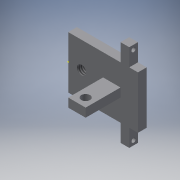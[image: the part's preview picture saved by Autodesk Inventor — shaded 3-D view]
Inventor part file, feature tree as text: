
AUTODESK INVENTOR PART (.ipt)
format: ipt  version: 2017 (Build 210142000, 142)  size: 150,016 bytes
history: native  units: in
note: dims shown in document units (in); Inventor stores cm internally (conversion verified against a paired STEP export)
features: sketch x7, hole x4, extrude x3, projected_geometry x2
ambient origin geometry x8: Origin, YZ Plane, XZ Plane, XY Plane, X Axis, Y Axis, Z Axis, Center Point
bodies: Solid1 (feature_tree)
feature tree (16):
  extrude  "Extrusion1"  Depth=1.0in
  extrude  "Extrusion2"  Depth=0.25in
  hole  "Hole1"  [1 undecoded]
  hole  "Hole3"  [1 undecoded]
  sketch  "Sketch6"  dims[d12=0.25in d13=0.5in d14=0.0in]
  sketch  "Sketch7"  dims[d15=0.06in d16=0.75in d17=0.375in d18=0.25in d19=0.5635in d20=1.0in d21=0.8108in d22=0.125in]
  extrude  "Extrusion3"  Depth=0.5in TaperAngle=0.0deg
  hole  "Hole4"  [1 undecoded]
  hole  "Hole5"  [1 undecoded]
  sketch  "Sketch1"  dims[d0=0.75in d2=1.0in]
  sketch  "Sketch2"  dims[d3=0.125in d4=0.25in]
  sketch  "Sketch3"  dims[d5=0.125in d6=0.0in d7=0.125in]
  projected_geometry  "Projected Loop1"
  sketch  "Sketch5"  dims[d10=0.25in d11=0.3125in]
  projected_geometry  "Projected Loop3"
  sketch  "Sketch8"  dims[d30=0.13in d31=0.75in d32=0.375in d33=0.25in d34=0.5635in d35=1.0in d36=0.8108in d37=0.125in d38=0.063in d39=0.25in d40=0.0in d41=0.0625in d42=0.0625in d43=0.06in d44=0.75in d45=0.375in d46=0.25in d47=0.5635in d48=1.0in d49=0.8108in d50=0.125in d51=0.125in d52=0.125in d53=0.75in d54=0.375in d55=0.25in d56=0.5635in d57=1.0in d58=0.8108in]
note: 4 required parameter values undecoded (feature->parameter linkage not recoverable at this tier; creation-order binding heuristic only, values carry confidence <= 0.55)
